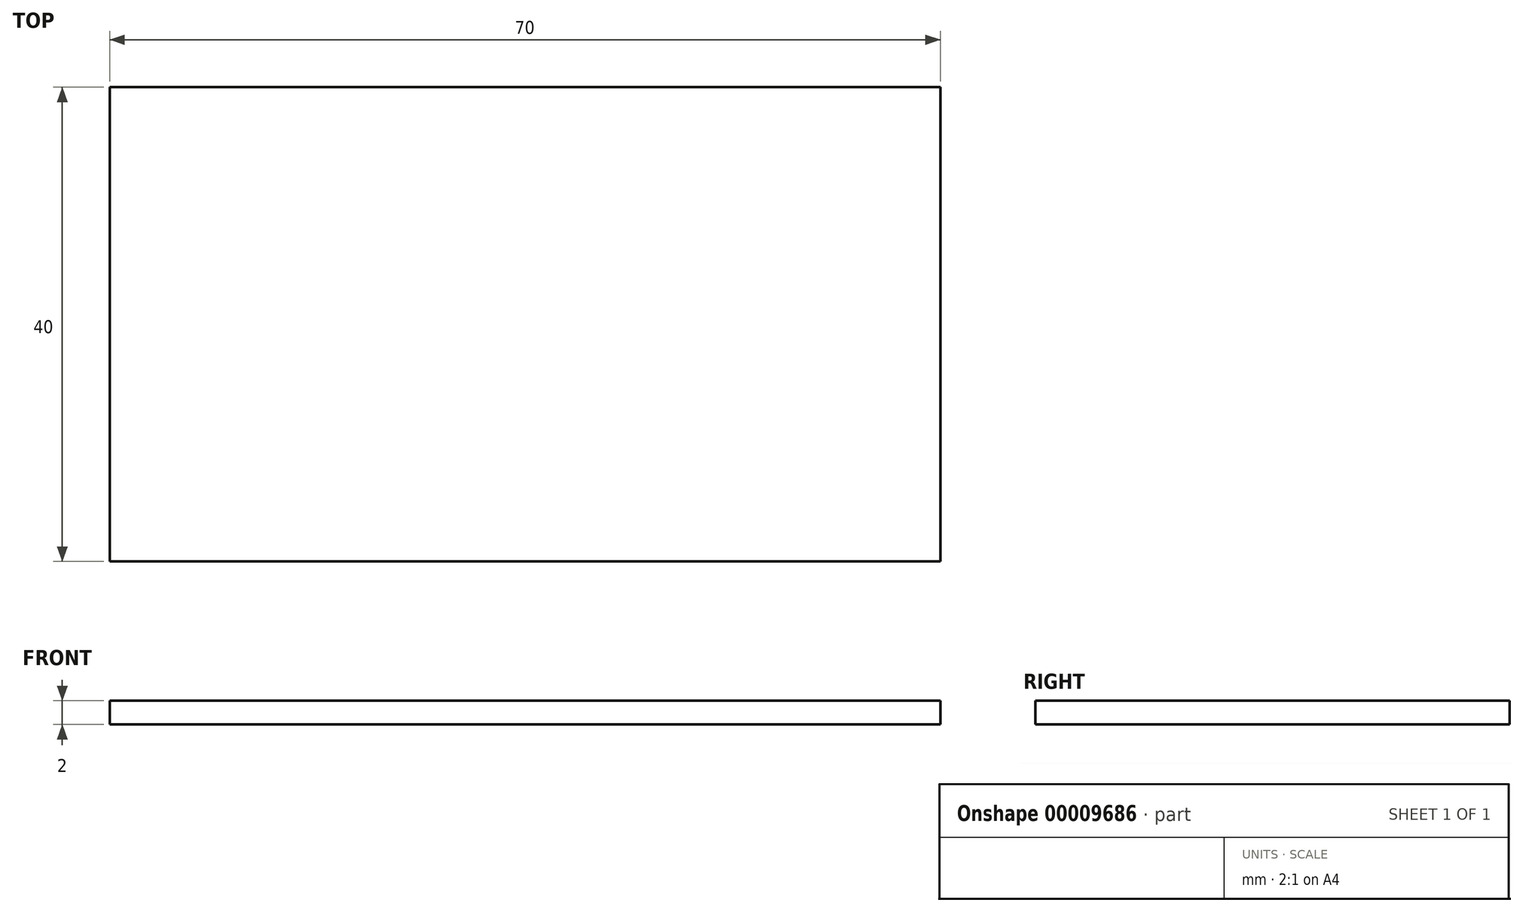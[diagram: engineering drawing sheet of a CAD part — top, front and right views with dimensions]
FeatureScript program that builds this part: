
annotation { "Feature Type Name" : "Feature", "Feature Type Description" : "" }
export const myFeature = defineFeature(function(context is Context, id is Id, definition is map)
    precondition{}
    {
        {
            var Q0;
            Q0=qCreatedBy(makeId("Top.planeOp"),FACE);
            var sketch = newSketch(context, id + "F0", { "sketchPlane" : qUnion([Q0])});
            skLineSegment(sketch, "E0.rect.bottom", {"start": v(-35, 20) * mm, "end": v(35, 20) * mm});
            skLineSegment(sketch, "E0.rect.top", {"start": v(-35, -20) * mm, "end": v(35, -20) * mm});
            skLineSegment(sketch, "E0.rect.left", {"start": v(-35, 20) * mm, "end": v(-35, -20) * mm});
            skLineSegment(sketch, "E0.rect.right", {"start": v(35, 20) * mm, "end": v(35, -20) * mm});
            skPoint(sketch, "E0.rect.middle", {"position": v(0, 0) * mm});
            skSolve(sketch);
        }
        {
            var Q0;
            Q0 = qSketchRegion(id + "F0", true);
            extrude(context, id + "F1", {"entities" : qUnion([Q0]), "depth" : 2 * mm});
        }
    });
